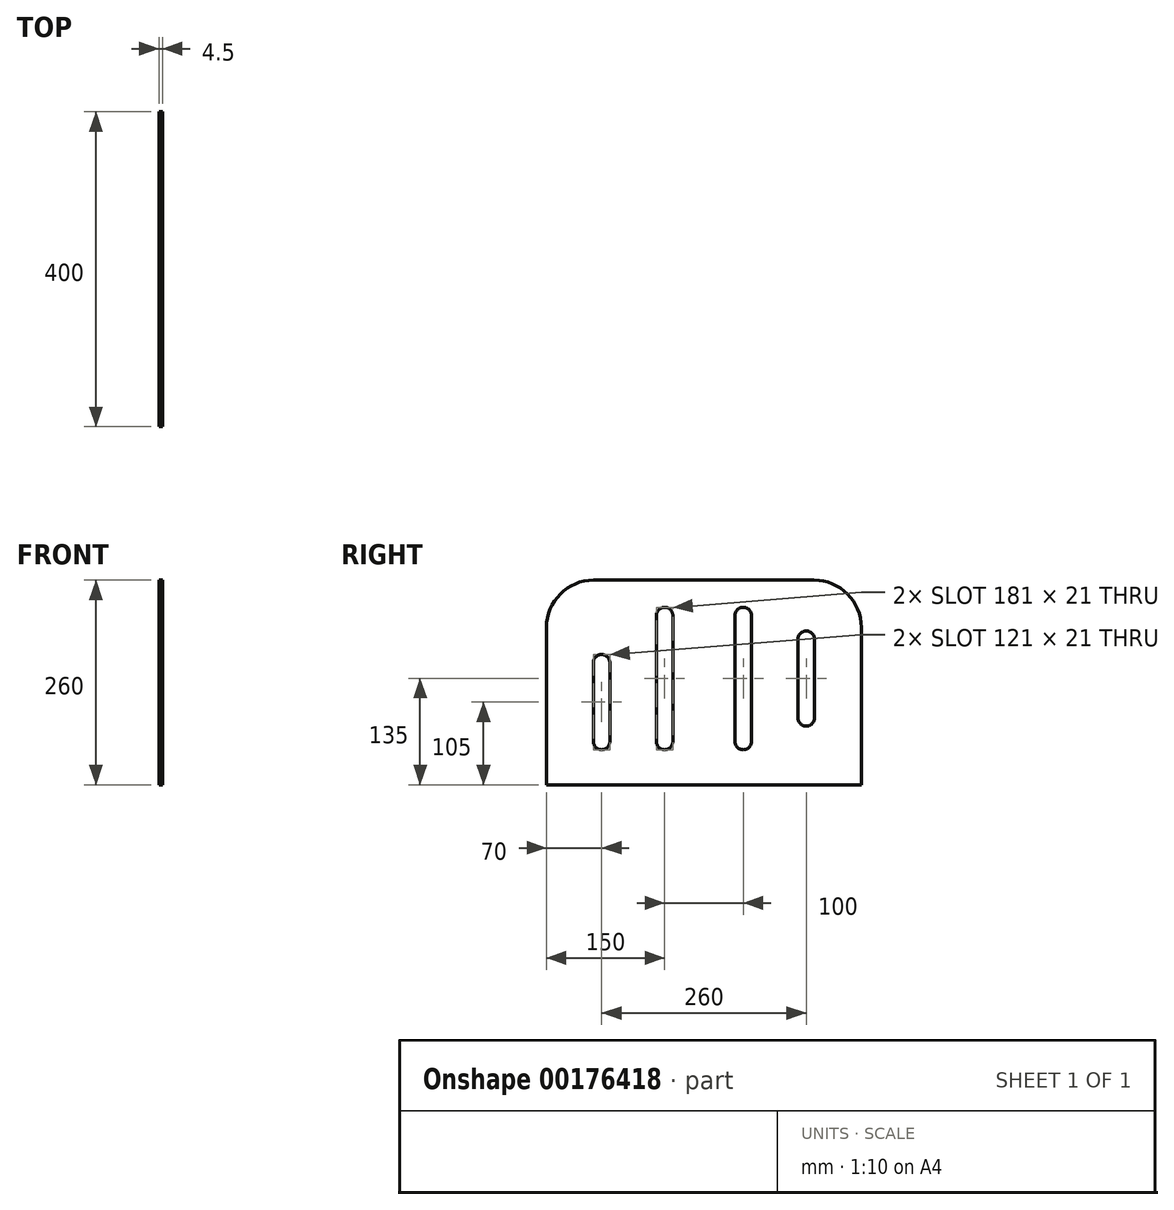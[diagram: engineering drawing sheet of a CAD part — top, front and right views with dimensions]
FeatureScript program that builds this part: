
annotation { "Feature Type Name" : "Feature", "Feature Type Description" : "" }
export const myFeature = defineFeature(function(context is Context, id is Id, definition is map)
    precondition{}
    {
        {
            var Q0;
            Q0=qCreatedBy(makeId("Right.planeOp"),FACE);
            var sketch = newSketch(context, id + "F0", { "sketchPlane" : qUnion([Q0])});
            skLineSegment(sketch, "E0", {"start": v(300, -710) * mm, "end": v(-100, -710) * mm});
            skLineSegment(sketch, "E1", {"start": v(300, -710) * mm, "end": v(300, -510) * mm});
            skLineSegment(sketch, "E2", {"start": v(-100, -510) * mm, "end": v(-100, -710) * mm});
            skArc(sketch, "E3", {"start": v(219.5, -625) * mm, "mid": v(230, -635.5) * mm, "end": v(240.5, -625) * mm});
            skLineSegment(sketch, "E4", {"start": v(-40, -450) * mm, "end": v(240, -450) * mm});
            skLineSegment(sketch, "E5", {"start": v(-100, -555) * mm, "end": v(300, -555) * mm, "construction": true});
            skLineSegment(sketch, "E6.trimOffspring", {"start": v(219.5, -525) * mm, "end": v(219.5, -625) * mm});
            skLineSegment(sketch, "E7.trimOffspring", {"start": v(240.5, -625) * mm, "end": v(240.5, -525) * mm});
            skLineSegment(sketch, "E8", {"start": v(39.5, -495) * mm, "end": v(39.5, -655) * mm});
            skArc(sketch, "E9", {"start": v(60.5, -495) * mm, "mid": v(50, -484.5) * mm, "end": v(39.5, -495) * mm});
            skArc(sketch, "E10", {"start": v(39.5, -655) * mm, "mid": v(50, -665.5) * mm, "end": v(60.5, -655) * mm});
            skLineSegment(sketch, "E11.trimOffspring", {"start": v(60.5, -655) * mm, "end": v(60.5, -495) * mm});
            skArc(sketch, "E12", {"start": v(-40.5, -655) * mm, "mid": v(-30, -665.5) * mm, "end": v(-19.5, -655) * mm});
            skArc(sketch, "E13", {"start": v(-19.5, -555) * mm, "mid": v(-30, -544.5) * mm, "end": v(-40.5, -555) * mm});
            skLineSegment(sketch, "E14.trimOffspring", {"start": v(-40.5, -555) * mm, "end": v(-40.5, -655) * mm});
            skLineSegment(sketch, "E15.trimOffspring", {"start": v(-19.5, -655) * mm, "end": v(-19.5, -555) * mm});
            skLineSegment(sketch, "E16", {"start": v(139.5, -495) * mm, "end": v(139.5, -655) * mm});
            skArc(sketch, "E17", {"start": v(160.5, -495) * mm, "mid": v(150, -484.5) * mm, "end": v(139.5, -495) * mm});
            skArc(sketch, "E18", {"start": v(139.5, -655) * mm, "mid": v(150, -665.5) * mm, "end": v(160.5, -655) * mm});
            skLineSegment(sketch, "E19.trimOffspring", {"start": v(160.5, -655) * mm, "end": v(160.5, -495) * mm});
            skArc(sketch, "E20", {"start": v(240.5, -525) * mm, "mid": v(230, -514.5) * mm, "end": v(219.5, -525) * mm});
            skPoint(sketch, "E21.end.orphan", {"position": v(0, 0) * mm});
            skPoint(sketch, "E22.visualSharp", {"position": v(-100, -450) * mm});
            skArc(sketch, "E22.filletArc", {"start": v(-40, -450) * mm, "mid": v(-82.43, -467.57) * mm, "end": v(-100, -510) * mm});
            skPoint(sketch, "E23.visualSharp", {"position": v(300, -450) * mm});
            skArc(sketch, "E23.filletArc", {"start": v(300, -510) * mm, "mid": v(282.43, -467.57) * mm, "end": v(240, -450) * mm});
            skLineSegment(sketch, "E24", {"start": v(-100, -655) * mm, "end": v(300, -655) * mm, "construction": true});
            skLineSegment(sketch, "E25", {"start": v(-10.62, -495) * mm, "end": v(197.9, -495) * mm, "construction": true});
            skSolve(sketch);
        }
        {
            var Q0;
            {var subQ5=sQuery(id+"F0.wireOp",EDGE,"E0");Q0=makeQuery(id+"F0.imprint","IMPRINT",FACE,{"disambiguationData":[TD([[makeQuery(id+"F0.imprint","IMPRINT",EDGE,{"derivedFrom":subQ5}),-1.0]])]});}
            extrude(context, id + "F1", {"entities" : qUnion([Q0]), "oppositeDirection" : true, "depth" : 4.5 * mm});
        }
    });
